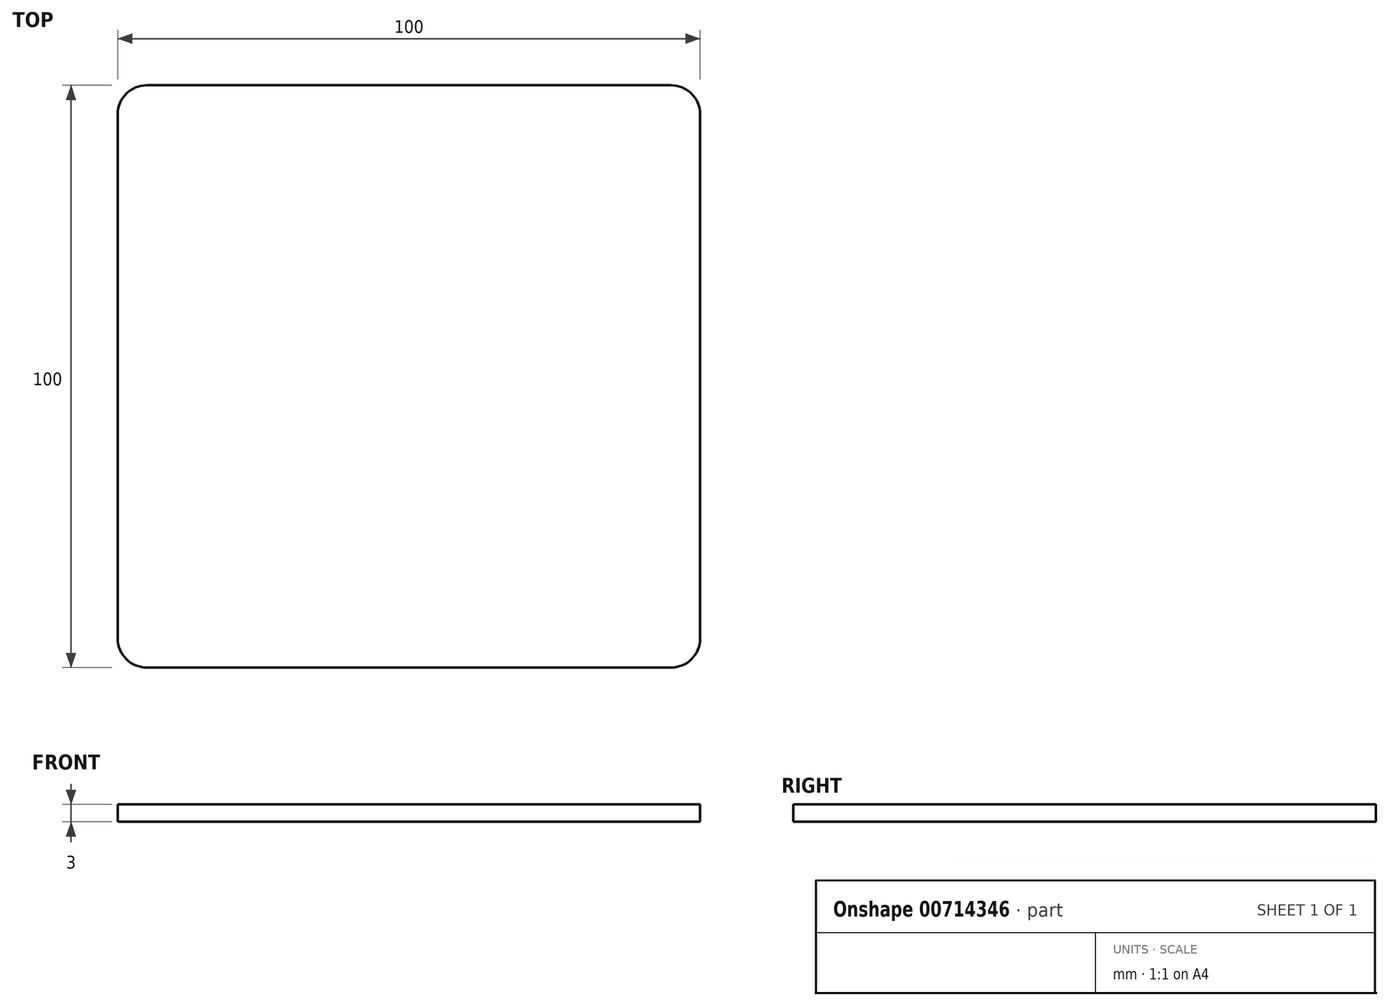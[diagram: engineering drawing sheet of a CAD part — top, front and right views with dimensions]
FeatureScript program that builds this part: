
annotation { "Feature Type Name" : "Feature", "Feature Type Description" : "" }
export const myFeature = defineFeature(function(context is Context, id is Id, definition is map)
    precondition{}
    {
        {
            var Q0;
            Q0=qCreatedBy(makeId("Top.planeOp"),FACE);
            var sketch = newSketch(context, id + "F0", { "sketchPlane" : qUnion([Q0])});
            skLineSegment(sketch, "E0.bottom", {"start": v(45, 50) * mm, "end": v(-45, 50) * mm});
            skLineSegment(sketch, "E0.top", {"start": v(45, -50) * mm, "end": v(-45, -50) * mm});
            skLineSegment(sketch, "E0.left", {"start": v(50, 45) * mm, "end": v(50, -45) * mm});
            skLineSegment(sketch, "E0.right", {"start": v(-50, 45) * mm, "end": v(-50, -45) * mm});
            skPoint(sketch, "E0.middle", {"position": v(0, 0) * mm});
            skPoint(sketch, "E1.visualSharp", {"position": v(-50, -50) * mm});
            skArc(sketch, "E1.filletArc", {"start": v(-50, -45) * mm, "mid": v(-48.54, -48.54) * mm, "end": v(-45, -50) * mm});
            skPoint(sketch, "E2.visualSharp", {"position": v(50, -50) * mm});
            skArc(sketch, "E2.filletArc", {"start": v(45, -50) * mm, "mid": v(48.54, -48.54) * mm, "end": v(50, -45) * mm});
            skPoint(sketch, "E3.visualSharp", {"position": v(50, 50) * mm});
            skArc(sketch, "E3.filletArc", {"start": v(50, 45) * mm, "mid": v(48.54, 48.54) * mm, "end": v(45, 50) * mm});
            skPoint(sketch, "E4.visualSharp", {"position": v(-50, 50) * mm});
            skArc(sketch, "E4.filletArc", {"start": v(-45, 50) * mm, "mid": v(-48.54, 48.54) * mm, "end": v(-50, 45) * mm});
            skLineSegment(sketch, "E5", {"start": v(0, 0) * mm, "end": v(0, -50) * mm, "construction": true});
            skLineSegment(sketch, "E6", {"start": v(0, 0) * mm, "end": v(-50, 0) * mm, "construction": true});
            skSolve(sketch);
        }
        {
            var Q0;
            Q0=makeQuery(id+"F0.imprint","IMPRINT",FACE,{"disambiguationData":[TD([[makeQuery(id+"F0.imprint","IMPRINT",EDGE,{"derivedFrom":sQuery(id+"F0.wireOp",EDGE,"E0.bottom")}),1.0]])]});
            extrude(context, id + "F1", {"entities" : qUnion([Q0]), "depth" : 3 * mm, "offsetDistance" : 25 * mm});
        }
    });
